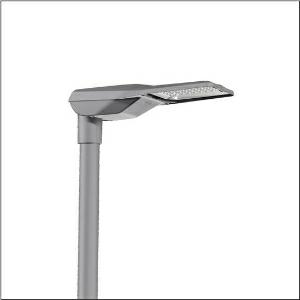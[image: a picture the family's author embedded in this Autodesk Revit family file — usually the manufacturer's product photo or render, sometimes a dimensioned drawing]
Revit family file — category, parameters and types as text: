
# Revit family: streetlight_sl_21_iq_mini___st1_5a_5xe2p31d08gb_fdd6
name_source: partatom
category: Lighting Fixtures
units: mm (PartAtom-declared; Revit-internal decimal feet)

## family parameters
Cut with Voids When Loaded = No
Host = Face
Light Source = No
Part Type = Normal
Room Calculation Point = No
Round Connector Dimension = Use Diameter
Shared = No

## types (1)
- --- (1 x LED, 5580 lm, 37.1 W, 3000K)
    Apparent Load = 37 VA
    CIE Flux Codes = 22 53 95 100 100
    Color Rendering = 70
    Color Temperature = 3000K
    Default Elevation = 1800 mm
    Description = Streetlight SL 21 iQ mini, mast luminaire, primary light control with lens, of PMMA, primary optical cover: cover, of toughened safety glass, transparent, light distribution: ST1.5a, light emission: direct distribution, primary light characteristic: asymmetric, installation type: post-top, side-entry, LED, High Power LED, rated luminous flux: 5.580lm, luminous efficacy: 150lm/W, light colour: 730, colour temperature: 3000K, control gear: iQ-Comfort, control: Auto-Match, Temp-Guard, Lumen-Switch, Night-Set, Smart-Wire, Light-Fading, Desk-Remote (wireless, voltage-free reading and setting of iQ features in the workshop via application-optimized NFC function/RFID function), optimised constant luminous flux control (CLO 2.0), pre-setting: linear dimming characteristic, mains connection: 220..240V, AC, 50/60Hz, start of lifetime: 37W, end of service life: 39W, reduction: 18W, luminaire housing, of diecast aluminium, powder-coated, SITECO metallic grey (DB 702S), corrosivity category C5 high according to DIN EN ISO 12944, please order mast flange separately, inclination adjustable: 0°, 5°, 10°, 15°, sealing non-destructively replaceable, multi-level sealing system, length: 628mm, width: 235mm, height: 110mm, mast flange for spigot size: 42mm (side-entry): 5XC10008XM4, 60/48mm (side-entry/post-top): 5XC10108XM2, 76/60mm (side-entry/post-top): 5XC10108XM1, mounting height: 4..8m, protection rating (complete): IP66, insulation class (complete): insulation class II (safety insulation), certification: CE, ENEC, ENEC+, VDE, impact resistance: IK10, permissible operating ambient temperature for outdoor applications: -40..+50°C, standard-compliant lighting for roads and squares, packaging unit: 1 piece

Light Distribution: ST1.5a
    Height = 110 mm
    Lamp = 1 x LED
    Lamp Light Flux = 5580 lm
    Lamp Power = 37.1 W
    Lamp count = 1
    Length = 625 mm
    Luminous efficacy = 150 lm/W
    Manufacturer = Siteco
    ModVariant = No
    Model = 5XE2P31D08GB
    Number of Poles = 1
    OnlyDefault = Yes
    Power Factor = 1
    Product Name = Streetlight SL 21 iQ mini | ST1.5a
    Product group = mast luminaire | pylon top
    ProductGroupID = 6100
    Protection Class = Protection class II
    Protection Degree = IP 66
    RLX_Detail_Level = 1
    RLX_Emergency_Light_Flux = 0 lm
    RLX_Emergency_Type = 0
    RLX_Emergency_Type_DB = No
    RlxData = <blob elided: 29833 chars, md5=61652990>
    Socket = socket
    Standby Power = 0 W
    System Light Flux = 5580 lm
    System Power = 37 W
    Type Comments = factory setting: luminous flux: 100 % | dim-lin: 254 | 385 mA
    Type Image = l_1003519.jpg
    URL = http://relux.com
    VarID = @adj_175351
    Voltage = 0 V
    Weight = 0.00 kg
    Width = 234 mm

## geometry (parser evidence)
native form markers: Blend x4, Sweep x10
no freeform markers — native parametric forms only
